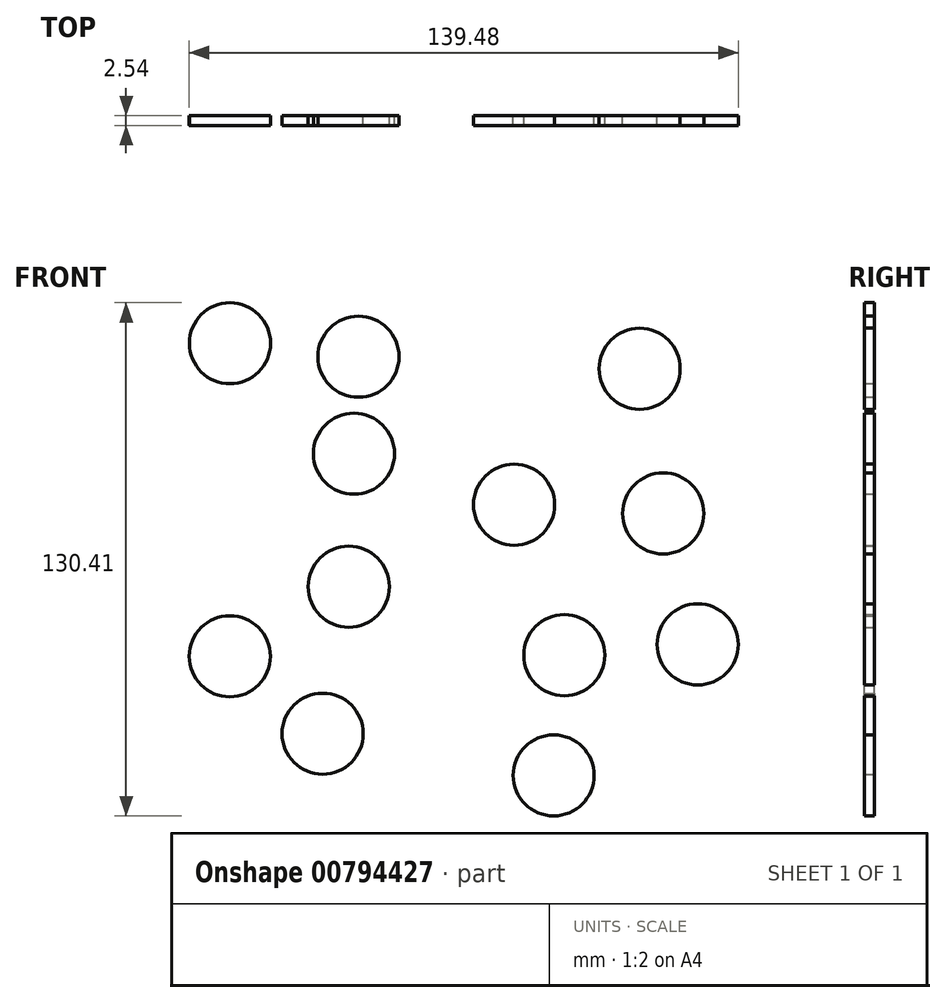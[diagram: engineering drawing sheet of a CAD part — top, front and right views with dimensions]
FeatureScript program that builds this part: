
annotation { "Feature Type Name" : "Feature", "Feature Type Description" : "" }
export const myFeature = defineFeature(function(context is Context, id is Id, definition is map)
    precondition{}
    {
        {
            var Q0;
            Q0=qCreatedBy(makeId("Front.planeOp"),FACE);
            var sketch = newSketch(context, id + "F0", { "sketchPlane" : qUnion([Q0])});
            skCircle(sketch, "E0", {"center": v(-61.2, 52.04) * mm, "radius": 10.3 * mm});
            skCircle(sketch, "E1", {"center": v(-28.55, 48.6) * mm, "radius": 10.3 * mm});
            skCircle(sketch, "E2", {"center": v(42.87, 45.54) * mm, "radius": 10.3 * mm});
            skCircle(sketch, "E3", {"center": v(-29.7, 23.96) * mm, "radius": 10.3 * mm});
            skCircle(sketch, "E4", {"center": v(10.98, 10.98) * mm, "radius": 10.3 * mm});
            skCircle(sketch, "E5", {"center": v(-31.03, -9.83) * mm, "radius": 10.3 * mm});
            skSolve(sketch);
        }
        {
            var Q0;
            Q0 = qSketchRegion(id + "F0", true);
            extrude(context, id + "F1", {"entities" : qUnion([Q0]), "depth" : 2.54 * mm, "offsetDistance" : 25.4 * mm});
        }
        {
            var Q0;
            Q0=qCreatedBy(makeId("Front.planeOp"),FACE);
            var sketch = newSketch(context, id + "F2", { "sketchPlane" : qUnion([Q0])});
            skCircle(sketch, "E6", {"center": v(23.75, -27.22) * mm, "radius": 10.3 * mm});
            skCircle(sketch, "E7", {"center": v(-61.26, -27.53) * mm, "radius": 10.3 * mm});
            skCircle(sketch, "E8", {"center": v(21.02, -57.78) * mm, "radius": 10.3 * mm});
            skCircle(sketch, "E9", {"center": v(-37.66, -47.19) * mm, "radius": 10.3 * mm});
            skCircle(sketch, "E10", {"center": v(57.63, -24.5) * mm, "radius": 10.3 * mm});
            skCircle(sketch, "E11", {"center": v(48.85, 8.77) * mm, "radius": 10.3 * mm});
            skSolve(sketch);
        }
        {
            var Q0;
            Q0 = qSketchRegion(id + "F2", true);
            extrude(context, id + "F3", {"entities" : qUnion([Q0]), "depth" : 2.54 * mm, "offsetDistance" : 25.4 * mm});
        }
    });
